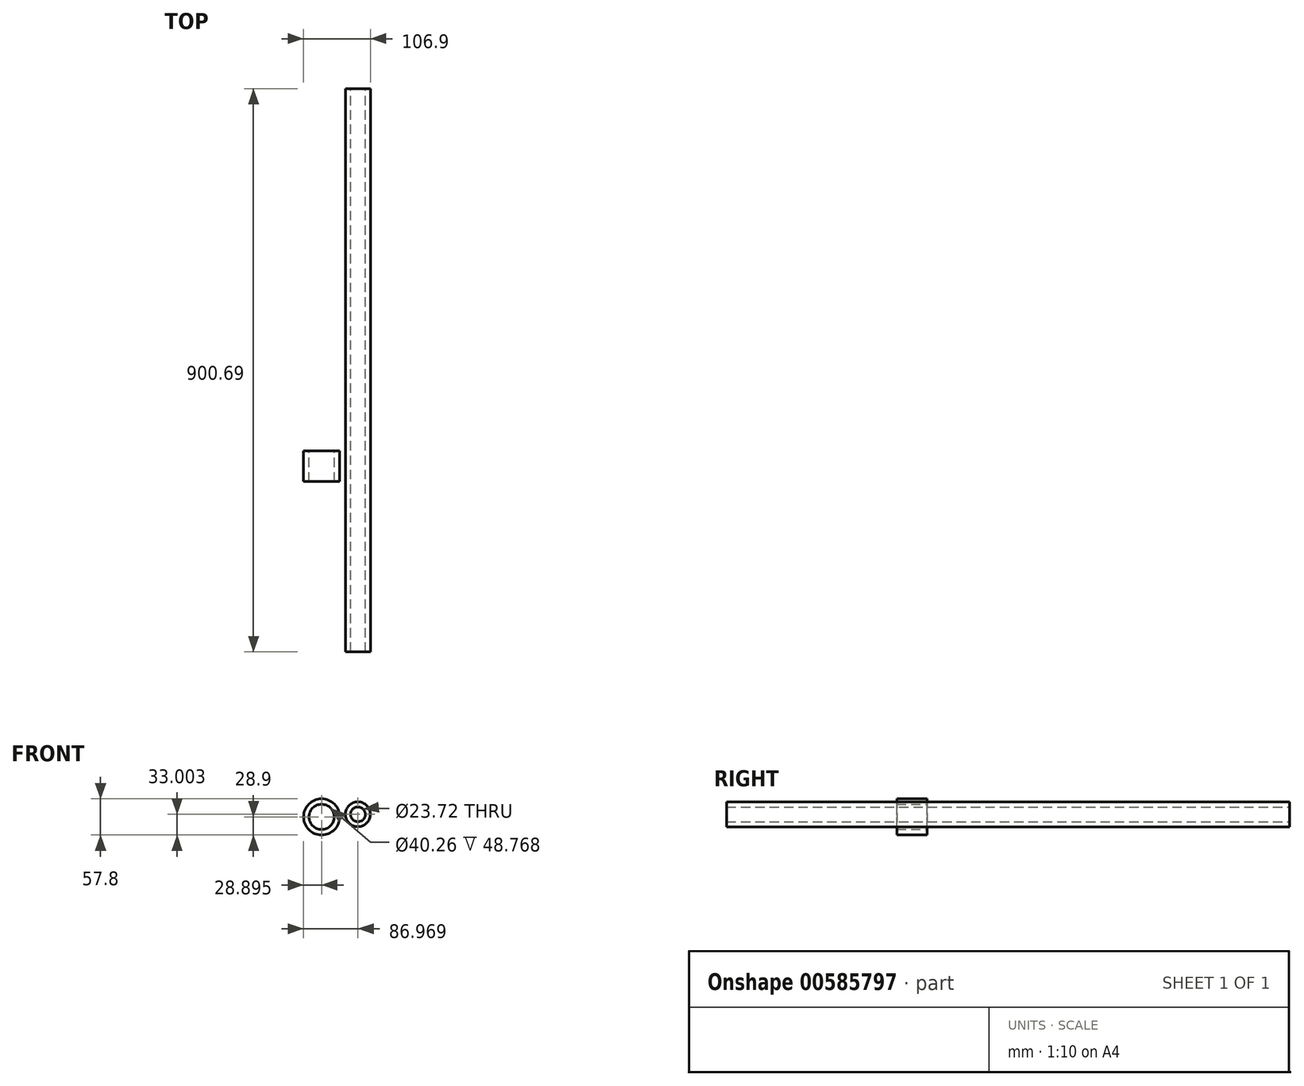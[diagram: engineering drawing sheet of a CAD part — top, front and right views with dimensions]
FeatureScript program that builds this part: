
annotation { "Feature Type Name" : "Feature", "Feature Type Description" : "" }
export const myFeature = defineFeature(function(context is Context, id is Id, definition is map)
    precondition{}
    {
        {
            var Q0;
            Q0=qCreatedBy(makeId("Front.planeOp"),FACE);
            var sketch = newSketch(context, id + "F0", { "sketchPlane" : qUnion([Q0])});
            skCircle(sketch, "E0", {"center": v(-39.3, 30.3) * mm, "radius": 20.13 * mm});
            skCircle(sketch, "E1", {"center": v(-39.3, 30.3) * mm, "radius": 28.9 * mm});
            skSolve(sketch);
        }
        {
            var Q0;
            Q0=makeQuery(id+"F0.imprint","IMPRINT",FACE,{"disambiguationData":[TD([[makeQuery(id+"F0.imprint","IMPRINT",EDGE,{"derivedFrom":sQuery(id+"F0.wireOp",EDGE,"E0")}),-1.0]])]});
            extrude(context, id + "F1", {"entities" : qUnion([Q0]), "depth" : 48.77 * mm, "offsetDistance" : 25.4 * mm});
        }
        {
            var Q0;
            Q0=qCreatedBy(makeId("Front.planeOp"),FACE);
            var sketch = newSketch(context, id + "F2", { "sketchPlane" : qUnion([Q0])});
            skCircle(sketch, "E2", {"center": v(18.78, 34.4) * mm, "radius": 19.93 * mm});
            skCircle(sketch, "E3", {"center": v(18.78, 34.4) * mm, "radius": 11.86 * mm});
            skSolve(sketch);
        }
        {
            var Q0;
            Q0=makeQuery(id+"F2.imprint","IMPRINT",FACE,{"disambiguationData":[TD([[makeQuery(id+"F2.imprint","IMPRINT",EDGE,{"derivedFrom":sQuery(id+"F2.wireOp",EDGE,"E2")}),1.0]])]});
            extrude(context, id + "F3", {"entities" : qUnion([Q0]), "depth" : 155.2 * mm, "offsetDistance" : 25.4 * mm});
        }
        {
            var Q0;
            Q0=makeQuery(id+"F3.opExtrude","CAP_FACE",FACE,{"disambiguationData":[OSD([sQuery(id+"F2.wireOp",EDGE,"E2"),sQuery(id+"F2.wireOp",EDGE,"E3")])],"isStart":false});
            extrude(context, id + "F4", {"entities" : qUnion([Q0]), "operationType" : NewBodyOperationType.ADD, "depth" : 165.86 * mm, "offsetDistance" : 25.4 * mm});
        }
        {
            var Q0;
            Q0=makeQuery(id+"F3.opExtrude","CAP_FACE",FACE,{"disambiguationData":[OSD([sQuery(id+"F2.wireOp",EDGE,"E2"),sQuery(id+"F2.wireOp",EDGE,"E3")])],"isStart":true});
            extrude(context, id + "F5", {"entities" : qUnion([Q0]), "operationType" : NewBodyOperationType.ADD, "depth" : 287.53 * mm, "offsetDistance" : 25.4 * mm});
        }
        {
            var Q0;
            Q0=makeQuery(id+"F5.opExtrude","CAP_FACE",FACE,{"disambiguationData":[OSD([sQuery(id+"F2.wireOp",EDGE,"E2"),sQuery(id+"F2.wireOp",EDGE,"E3")])],"isStart":false});
            extrude(context, id + "F6", {"entities" : qUnion([Q0]), "operationType" : NewBodyOperationType.ADD, "depth" : 292.1 * mm, "offsetDistance" : 25.4 * mm});
        }
    });
